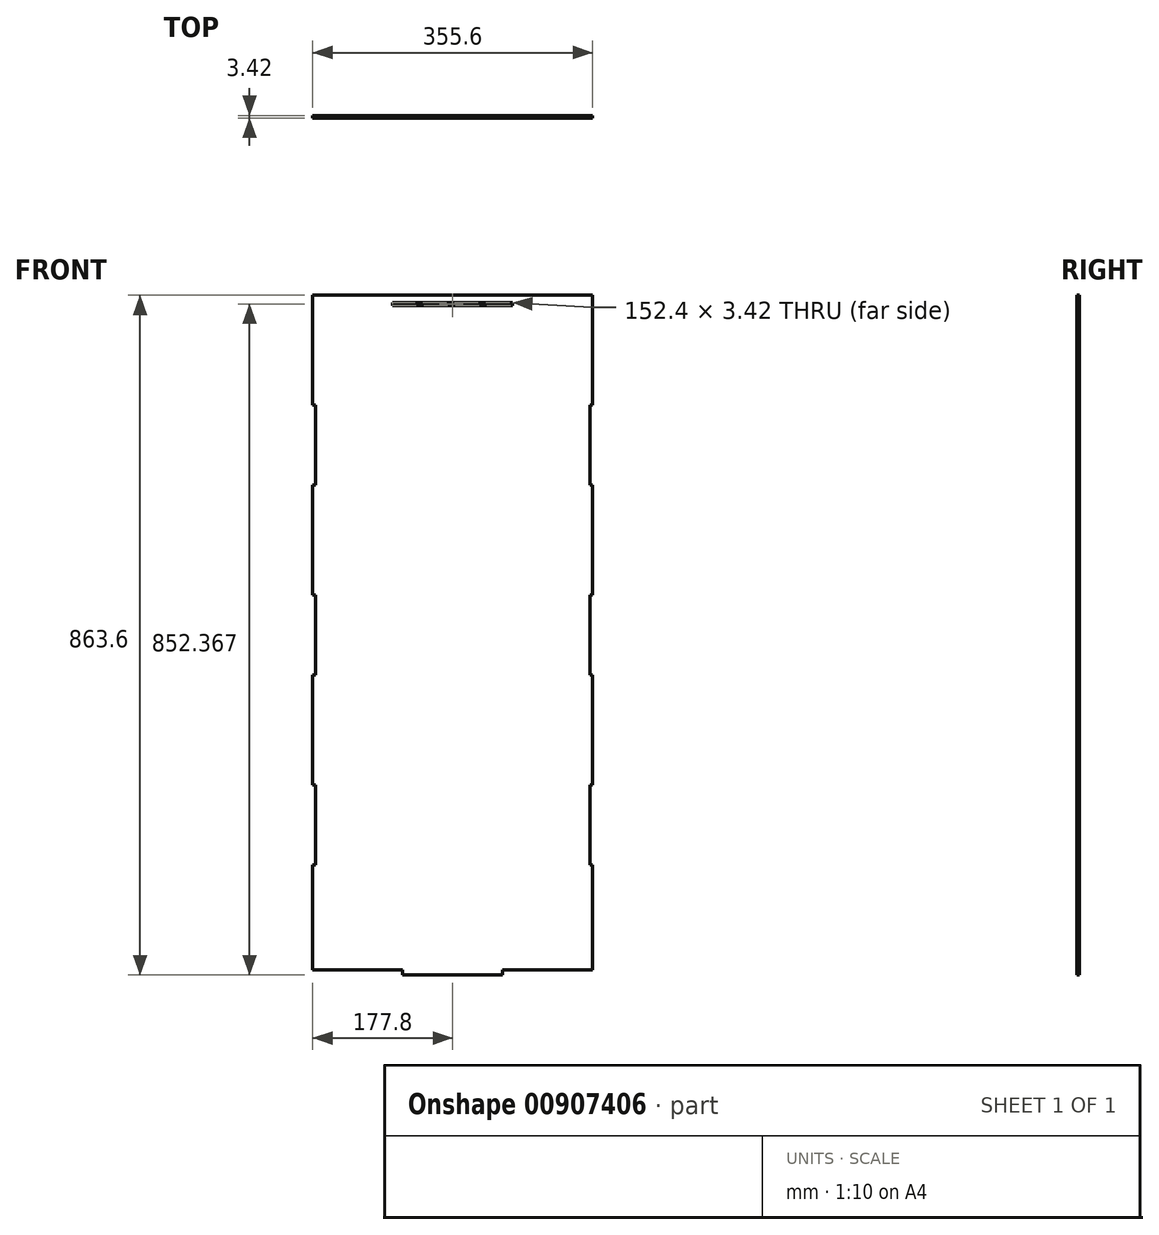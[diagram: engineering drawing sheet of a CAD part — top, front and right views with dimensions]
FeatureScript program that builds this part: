
annotation { "Feature Type Name" : "Feature", "Feature Type Description" : "" }
export const myFeature = defineFeature(function(context is Context, id is Id, definition is map)
    precondition{}
    {
        {
            var Q0;
            Q0=qCreatedBy(makeId("Front.planeOp"),FACE);
            var sketch = newSketch(context, id + "F0", { "sketchPlane" : qUnion([Q0])});
            skLineSegment(sketch, "E0", {"start": v(-63.5, 0) * mm, "end": v(-63.5, -6.35) * mm});
            skLineSegment(sketch, "E1", {"start": v(-63.5, -6.35) * mm, "end": v(63.5, -6.35) * mm});
            skLineSegment(sketch, "E2", {"start": v(63.5, -6.35) * mm, "end": v(63.5, 0) * mm});
            skLineSegment(sketch, "E3", {"start": v(-177.8, 0) * mm, "end": v(-63.5, 0) * mm});
            skLineSegment(sketch, "E4", {"start": v(63.5, 0) * mm, "end": v(177.8, 0) * mm});
            skLineSegment(sketch, "E5", {"start": v(-177.8, 0) * mm, "end": v(-177.8, 133.35) * mm});
            skLineSegment(sketch, "E6", {"start": v(-177.8, 133.35) * mm, "end": v(-174.38, 133.35) * mm});
            skLineSegment(sketch, "E7", {"start": v(-174.38, 133.35) * mm, "end": v(-174.38, 234.95) * mm});
            skLineSegment(sketch, "E8", {"start": v(-174.38, 234.95) * mm, "end": v(-177.8, 234.95) * mm});
            skLineSegment(sketch, "E9", {"start": v(-177.8, 234.95) * mm, "end": v(-177.8, 374.65) * mm});
            skLineSegment(sketch, "E10", {"start": v(-177.8, 374.65) * mm, "end": v(-174.38, 374.65) * mm});
            skLineSegment(sketch, "E11", {"start": v(-174.38, 374.65) * mm, "end": v(-174.38, 476.25) * mm});
            skLineSegment(sketch, "E12", {"start": v(-174.38, 476.25) * mm, "end": v(-177.8, 476.25) * mm});
            skLineSegment(sketch, "E13", {"start": v(-177.8, 476.25) * mm, "end": v(-177.8, 615.95) * mm});
            skLineSegment(sketch, "E14", {"start": v(-177.8, 615.95) * mm, "end": v(-174.38, 615.95) * mm});
            skLineSegment(sketch, "E15", {"start": v(-174.38, 615.95) * mm, "end": v(-174.38, 717.55) * mm});
            skLineSegment(sketch, "E16", {"start": v(-174.38, 717.55) * mm, "end": v(-177.8, 717.55) * mm});
            skLineSegment(sketch, "E17", {"start": v(-177.8, 717.55) * mm, "end": v(-177.8, 857.25) * mm});
            skLineSegment(sketch, "E18", {"start": v(-177.8, 857.25) * mm, "end": v(-76.2, 857.25) * mm});
            skLineSegment(sketch, "E19", {"start": v(-76.2, 847.73) * mm, "end": v(-76.2, 844.3) * mm});
            skLineSegment(sketch, "E20", {"start": v(-76.2, 844.3) * mm, "end": v(76.2, 844.3) * mm});
            skLineSegment(sketch, "E21", {"start": v(76.2, 844.3) * mm, "end": v(76.2, 847.73) * mm});
            skLineSegment(sketch, "E22", {"start": v(76.2, 857.25) * mm, "end": v(177.8, 857.25) * mm});
            skLineSegment(sketch, "E23", {"start": v(0, 844.3) * mm, "end": v(0, 0) * mm, "construction": true});
            skLineSegment(sketch, "E24.MirrorCS", {"start": v(177.8, 374.65) * mm, "end": v(174.38, 374.65) * mm});
            skLineSegment(sketch, "E25.MirrorCS", {"start": v(174.38, 717.55) * mm, "end": v(177.8, 717.55) * mm});
            skLineSegment(sketch, "E26.MirrorCS", {"start": v(174.38, 476.25) * mm, "end": v(177.8, 476.25) * mm});
            skLineSegment(sketch, "E27.MirrorCS", {"start": v(177.8, 133.35) * mm, "end": v(174.38, 133.35) * mm});
            skLineSegment(sketch, "E28.MirrorCS", {"start": v(174.38, 234.95) * mm, "end": v(177.8, 234.95) * mm});
            skLineSegment(sketch, "E29.MirrorCS", {"start": v(177.8, 615.95) * mm, "end": v(174.38, 615.95) * mm});
            skLineSegment(sketch, "E30.MirrorCS", {"start": v(174.38, 133.35) * mm, "end": v(174.38, 234.95) * mm});
            skLineSegment(sketch, "E31.MirrorCS", {"start": v(174.38, 615.95) * mm, "end": v(174.38, 717.55) * mm});
            skLineSegment(sketch, "E32.MirrorCS", {"start": v(174.38, 374.65) * mm, "end": v(174.38, 476.25) * mm});
            skLineSegment(sketch, "E33.MirrorCS", {"start": v(177.8, 0) * mm, "end": v(177.8, 133.35) * mm});
            skLineSegment(sketch, "E34.MirrorCS", {"start": v(177.8, 717.55) * mm, "end": v(177.8, 857.25) * mm});
            skLineSegment(sketch, "E35.MirrorCS", {"start": v(177.8, 476.25) * mm, "end": v(177.8, 615.95) * mm});
            skLineSegment(sketch, "E36.MirrorCS", {"start": v(177.8, 234.95) * mm, "end": v(177.8, 374.65) * mm});
            skLineSegment(sketch, "E37", {"start": v(-76.2, 857.25) * mm, "end": v(76.2, 857.25) * mm});
            skLineSegment(sketch, "E38.0", {"start": v(-76.2, 847.73) * mm, "end": v(76.2, 847.73) * mm});
            skSolve(sketch);
        }
        {
            var Q0;
            Q0=makeQuery(id+"F0.imprint","IMPRINT",FACE,{"disambiguationData":[TD([[makeQuery(id+"F0.imprint","IMPRINT",EDGE,{"derivedFrom":sQuery(id+"F0.wireOp",EDGE,"E0")}),1.0]])]});
            extrude(context, id + "F1", {"entities" : qUnion([Q0]), "depth" : 3.42 * mm, "offsetDistance" : 25.4 * mm});
        }
    });
